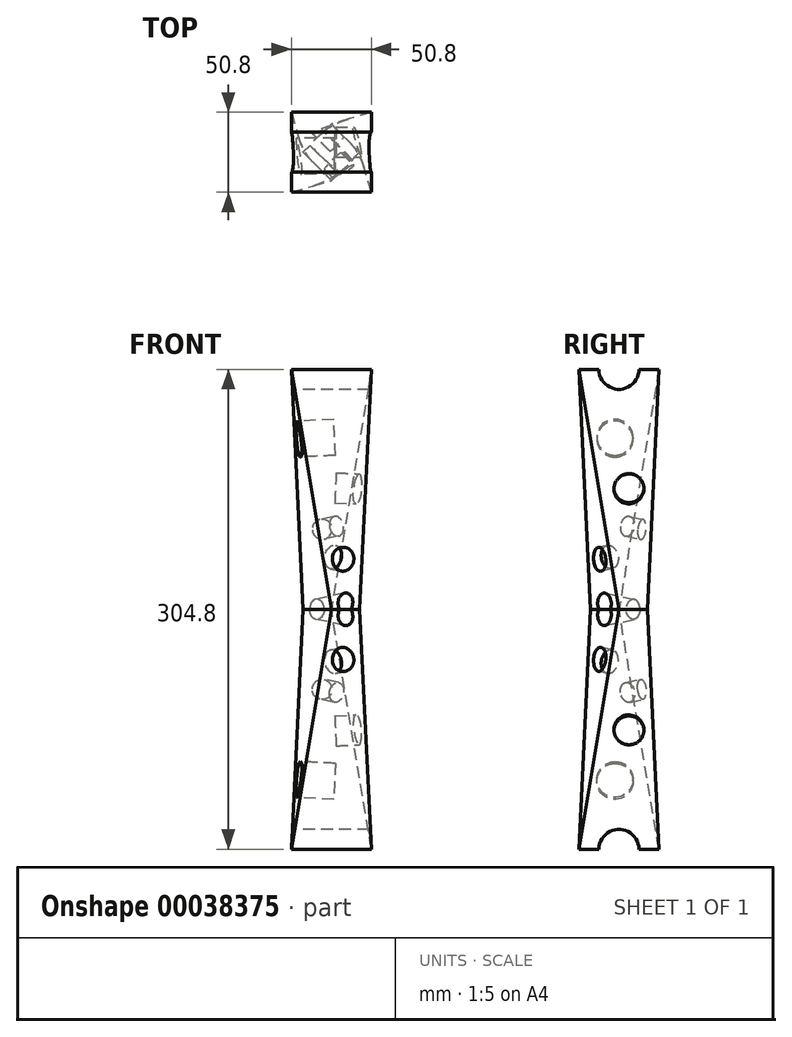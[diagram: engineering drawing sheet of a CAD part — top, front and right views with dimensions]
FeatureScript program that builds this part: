
annotation { "Feature Type Name" : "Feature", "Feature Type Description" : "" }
export const myFeature = defineFeature(function(context is Context, id is Id, definition is map)
    precondition{}
    {
        {
            var Q0;
            Q0=qCreatedBy(makeId("Top.planeOp"),FACE);
            var sketch = newSketch(context, id + "F0", { "sketchPlane" : qUnion([Q0])});
            skLineSegment(sketch, "E0.bottom", {"start": v(0, 0) * mm, "end": v(50.8, 0) * mm});
            skLineSegment(sketch, "E0.top", {"start": v(0, 50.8) * mm, "end": v(50.8, 50.8) * mm});
            skLineSegment(sketch, "E0.left", {"start": v(0, 0) * mm, "end": v(0, 50.8) * mm});
            skLineSegment(sketch, "E0.right", {"start": v(50.8, 0) * mm, "end": v(50.8, 50.8) * mm});
            skSolve(sketch);
        }
        {
            var Q0;
            Q0=qCreatedBy(makeId("Top.planeOp"),FACE);
            cPlane(context, id + "F1", {"entities" : qUnion([Q0]), "cplaneType" : CPlaneType.OFFSET, "offset" : 152.4 * mm, "width" : 152.4 * mm, "height" : 152.4 * mm});
        }
        {
            var Q0;
            Q0=qCreatedBy(id+"F1.planeOp",FACE);
            var sketch = newSketch(context, id + "F2", { "sketchPlane" : qUnion([Q0])});
            skLineSegment(sketch, "E1", {"start": v(7.44, 25.4) * mm, "end": v(25.4, 7.44) * mm});
            skLineSegment(sketch, "E2", {"start": v(25.4, 7.44) * mm, "end": v(43.36, 25.4) * mm});
            skLineSegment(sketch, "E3", {"start": v(43.36, 25.4) * mm, "end": v(25.4, 43.36) * mm});
            skLineSegment(sketch, "E4", {"start": v(25.4, 43.36) * mm, "end": v(7.44, 25.4) * mm});
            skSolve(sketch);
        }
        {
            var Q0;
            Q0=makeQuery(id+"F0.imprint","IMPRINT",FACE,{"disambiguationData":[TD([[makeQuery(id+"F0.imprint","IMPRINT",EDGE,{"derivedFrom":sQuery(id+"F0.wireOp",EDGE,"E0.bottom")}),1.0]])]});
            var Q1;
            Q1=makeQuery(id+"F2.imprint","IMPRINT",FACE,{"disambiguationData":[TD([[makeQuery(id+"F2.imprint","IMPRINT",EDGE,{"derivedFrom":sQuery(id+"F2.wireOp",EDGE,"E1")}),1.0]])]});
            loft(context, id + "F3", {"sheetProfilesArray" : [{ "sheetProfileEntities" : qUnion([Q0]) }, { "sheetProfileEntities" : qUnion([Q1]) }]});
        }
        {
            var Q0;
            Q0=qCreatedBy(makeId("Right.planeOp"),FACE);
            var sketch = newSketch(context, id + "F4", { "sketchPlane" : qUnion([Q0])});
            skCircle(sketch, "E5", {"center": v(25.4, 0) * mm, "radius": 12.7 * mm});
            skSolve(sketch);
        }
        {
            var Q0;
            Q0 = qSketchRegion(id + "F4", true);
            extrude(context, id + "F5", {"entities" : qUnion([Q0]), "operationType" : NewBodyOperationType.REMOVE, "endBound" : BoundingType.THROUGH_ALL, "depth" : 25.4 * mm});
        }
        {
            var Q0;
            Q0=makeQuery(id+"F3.opLoft","MID_CAP_VERTEX",VERTEX,{"disambiguationData":[OSD([sQuery(id+"F2.wireOp",EDGE,"E3"),sQuery(id+"F2.wireOp",EDGE,"E4")])],"capPos":1.0});
            var Q1;
            Q1=makeQuery(id+"F3.opLoft","MID_CAP_VERTEX",VERTEX,{"disambiguationData":[OSD([sQuery(id+"F2.wireOp",EDGE,"E1"),sQuery(id+"F2.wireOp",EDGE,"E4")])],"capPos":1.0});
            var Q2;
            Q2=makeQuery(id+"F3.opLoft","MID_CAP_VERTEX",VERTEX,{"disambiguationData":[OSD([sQuery(id+"F0.wireOp",EDGE,"E0.top"),sQuery(id+"F0.wireOp",EDGE,"E0.left")])],"capPos":0.0});
            cPlane(context, id + "F6", {"entities" : qUnion([Q0, Q1, Q2]), "cplaneType" : CPlaneType.THREE_POINT, "offset" : 152.4 * mm, "width" : 152.4 * mm, "height" : 152.4 * mm});
        }
        {
            var Q0;
            Q0=qCreatedBy(id+"F6.planeOp",FACE);
            var sketch = newSketch(context, id + "F7", { "sketchPlane" : qUnion([Q0])});
            skCircle(sketch, "E6", {"center": v(-57.53, 141.76) * mm, "radius": 6.35 * mm});
            skSolve(sketch);
        }
        {
            var Q0;
            Q0 = qSketchRegion(id + "F7", true);
            extrude(context, id + "F8", {"entities" : qUnion([Q0]), "operationType" : NewBodyOperationType.REMOVE, "endBound" : BoundingType.THROUGH_ALL, "oppositeDirection" : true, "depth" : 25.4 * mm});
        }
        {
            var Q0;
            Q0=makeQuery(id+"F3.opLoft","MID_CAP_VERTEX",VERTEX,{"disambiguationData":[OSD([sQuery(id+"F2.wireOp",EDGE,"E2"),sQuery(id+"F2.wireOp",EDGE,"E3")])],"capPos":1.0});
            var Q1;
            Q1=makeQuery(id+"F3.opLoft","MID_CAP_VERTEX",VERTEX,{"disambiguationData":[OSD([sQuery(id+"F0.wireOp",EDGE,"E0.bottom"),sQuery(id+"F0.wireOp",EDGE,"E0.right")])],"capPos":0.0});
            var Q2;
            Q2=makeQuery(id+"F3.opLoft","MID_CAP_VERTEX",VERTEX,{"disambiguationData":[OSD([sQuery(id+"F0.wireOp",EDGE,"E0.top"),sQuery(id+"F0.wireOp",EDGE,"E0.right")])],"capPos":0.0});
            cPlane(context, id + "F9", {"entities" : qUnion([Q0, Q1, Q2]), "cplaneType" : CPlaneType.THREE_POINT, "offset" : 152.4 * mm, "width" : 152.4 * mm, "height" : 152.4 * mm});
        }
        {
            var Q0;
            Q0=qCreatedBy(id+"F9.planeOp",FACE);
            var sketch = newSketch(context, id + "F10", { "sketchPlane" : qUnion([Q0])});
            skCircle(sketch, "E7", {"center": v(-31.75, 73.72) * mm, "radius": 9.53 * mm});
            skLineSegment(sketch, "E8", {"start": v(0, -2.48) * mm, "end": v(0, 150.1) * mm, "construction": true});
            skSolve(sketch);
        }
        {
            var Q0;
            Q0=makeQuery(id+"F10.imprint","IMPRINT",FACE,{"disambiguationData":[TD([[makeQuery(id+"F10.imprint","IMPRINT",EDGE,{"derivedFrom":sQuery(id+"F10.wireOp",EDGE,"E7")}),1.0]])]});
            extrude(context, id + "F11", {"entities" : qUnion([Q0]), "operationType" : NewBodyOperationType.REMOVE, "depth" : 19.05 * mm});
        }
        {
            var Q0;
            Q0=qCreatedBy(id+"F6.planeOp",FACE);
            var sketch = newSketch(context, id + "F12", { "sketchPlane" : qUnion([Q0])});
            skCircle(sketch, "E9", {"center": v(-56.3, 90.9) * mm, "radius": 6.35 * mm});
            skLineSegment(sketch, "E10", {"start": v(-34.71, -10.7) * mm, "end": v(-34.71, 140.51) * mm, "construction": true});
            skSolve(sketch);
        }
        {
            var Q0;
            Q0 = qSketchRegion(id + "F12", true);
            extrude(context, id + "F13", {"entities" : qUnion([Q0]), "operationType" : NewBodyOperationType.REMOVE, "oppositeDirection" : true, "depth" : 19.05 * mm});
        }
        {
            var Q0;
            Q0=makeQuery(id+"F3.opLoft","MID_CAP_VERTEX",VERTEX,{"disambiguationData":[OSD([sQuery(id+"F2.wireOp",EDGE,"E1"),sQuery(id+"F2.wireOp",EDGE,"E2")])],"capPos":1.0});
            var Q1;
            Q1=makeQuery(id+"F3.opLoft","MID_CAP_VERTEX",VERTEX,{"disambiguationData":[OSD([sQuery(id+"F2.wireOp",EDGE,"E2"),sQuery(id+"F2.wireOp",EDGE,"E3")])],"capPos":1.0});
            var Q2;
            Q2=makeQuery(id+"F3.opLoft","MID_CAP_VERTEX",VERTEX,{"disambiguationData":[OSD([sQuery(id+"F0.wireOp",EDGE,"E0.bottom"),sQuery(id+"F0.wireOp",EDGE,"E0.right")])],"capPos":0.0});
            cPlane(context, id + "F14", {"entities" : qUnion([Q0, Q1, Q2]), "cplaneType" : CPlaneType.THREE_POINT, "offset" : 152.4 * mm, "width" : 152.4 * mm, "height" : 152.4 * mm});
        }
        {
            var Q0;
            Q0=qCreatedBy(id+"F14.planeOp",FACE);
            var sketch = newSketch(context, id + "F15", { "sketchPlane" : qUnion([Q0])});
            skCircle(sketch, "E11", {"center": v(14.78, 120.65) * mm, "radius": 7.62 * mm});
            skLineSegment(sketch, "E12", {"start": v(0.8, 0) * mm, "end": v(0.8, 150.55) * mm, "construction": true});
            skSolve(sketch);
        }
        {
            var Q0;
            Q0=makeQuery(id+"F15.imprint","IMPRINT",FACE,{"disambiguationData":[TD([[makeQuery(id+"F15.imprint","IMPRINT",EDGE,{"derivedFrom":sQuery(id+"F15.wireOp",EDGE,"E11")}),1.0]])]});
            extrude(context, id + "F16", {"entities" : qUnion([Q0]), "operationType" : NewBodyOperationType.REMOVE, "oppositeDirection" : true, "depth" : 12.7 * mm});
        }
        {
            var Q0;
            Q0=makeQuery(id+"F3.opLoft","MID_CAP_VERTEX",VERTEX,{"disambiguationData":[OSD([sQuery(id+"F2.wireOp",EDGE,"E1"),sQuery(id+"F2.wireOp",EDGE,"E4")])],"capPos":1.0});
            var Q1;
            Q1=qCreatedBy(makeId("Origin.pointOp"),VERTEX);
            var Q2;
            Q2=makeQuery(id+"F3.opLoft","MID_CAP_VERTEX",VERTEX,{"disambiguationData":[OSD([sQuery(id+"F0.wireOp",EDGE,"E0.top"),sQuery(id+"F0.wireOp",EDGE,"E0.left")])],"capPos":0.0});
            cPlane(context, id + "F17", {"entities" : qUnion([Q0, Q1, Q2]), "cplaneType" : CPlaneType.THREE_POINT, "offset" : 152.4 * mm, "width" : 152.4 * mm, "height" : 152.4 * mm});
        }
        {
            var Q0;
            Q0=qCreatedBy(id+"F17.planeOp",FACE);
            var sketch = newSketch(context, id + "F18", { "sketchPlane" : qUnion([Q0])});
            skCircle(sketch, "E13", {"center": v(-22.86, 44.45) * mm, "radius": 11.43 * mm});
            skLineSegment(sketch, "E14", {"start": v(0, 0) * mm, "end": v(0, 154.5) * mm, "construction": true});
            skSolve(sketch);
        }
        {
            var Q0;
            Q0 = qSketchRegion(id + "F18", true);
            extrude(context, id + "F19", {"entities" : qUnion([Q0]), "operationType" : NewBodyOperationType.REMOVE, "oppositeDirection" : true, "depth" : 25.4 * mm});
        }
        {
            var Q0;
            Q0=makeQuery(id+"F3.opLoft","SWEPT_BODY",BODY,{"disambiguationData":[OSD([makeQuery(id+"F0.imprint","IMPRINT",FACE,{"disambiguationData":[TD([[makeQuery(id+"F0.imprint","IMPRINT",EDGE,{"derivedFrom":sQuery(id+"F0.wireOp",EDGE,"E0.bottom")}),1.0]])]}),makeQuery(id+"F2.imprint","IMPRINT",FACE,{"disambiguationData":[TD([[makeQuery(id+"F2.imprint","IMPRINT",EDGE,{"derivedFrom":sQuery(id+"F2.wireOp",EDGE,"E1")}),1.0]])]})])]});
            var Q1;
            Q1=qCreatedBy(id+"F1.planeOp",FACE);
            mirror(context, id + "F20", {"operationType" : NewBodyOperationType.ADD, "entities" : qUnion([Q0]), "mirrorPlane" : qUnion([Q1])});
        }
    });
